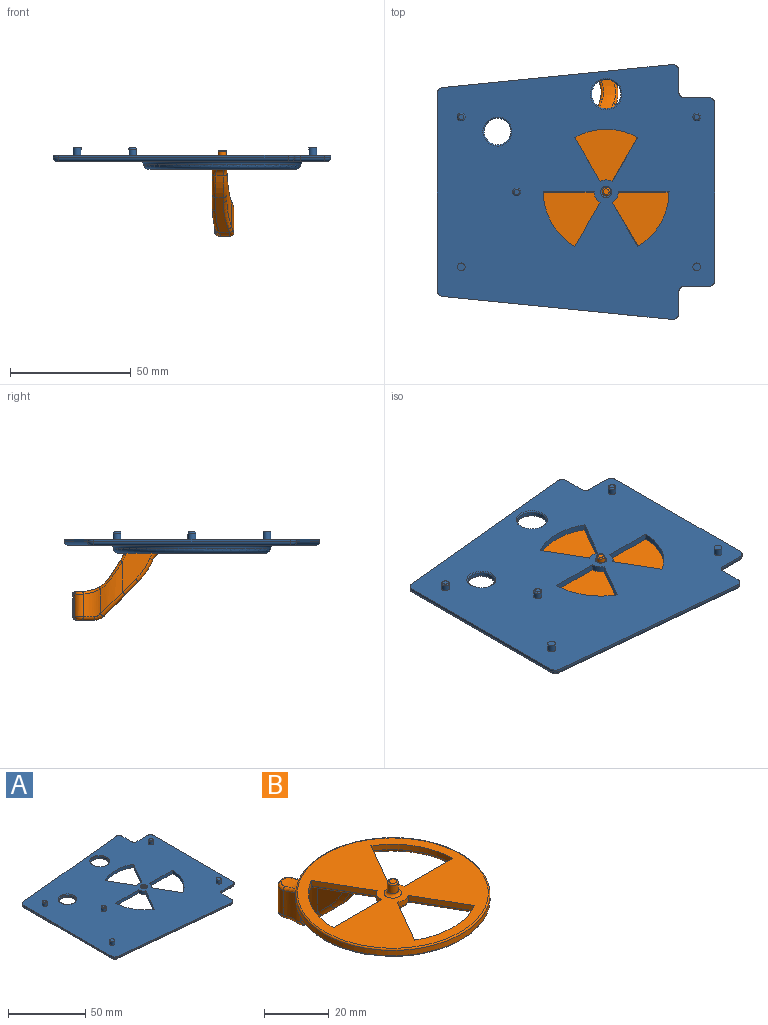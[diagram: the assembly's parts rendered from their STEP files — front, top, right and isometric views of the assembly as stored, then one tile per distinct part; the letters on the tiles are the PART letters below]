
ASSEMBLY  parts=2 mates=1
PART A: 74 faces, bbox 115x105.5x8.8 mm
  f0: plane 60.25x60.25mm, normal (0,0,-1), area 1802.9mm2, adj f9,f10,f11,f12,f13,f14,f15,f16
  f1: plane 112x102.48mm, normal (0,0,-1), area 6289.5mm2, adj f34,f35,f36,f37,f38,f39,f40,f41
  f2: plane 81.48x1mm, normal (-1,0,0), area 81.5mm2, adj f25,f26,f33,f40
  f3: plane 95x9.5mm, normal (-0.1,-1,0), area 95.5mm2, adj f25,f26,f27,f44
  f4: plane 8.74x1mm, normal (1,0,0), area 8.7mm2, adj f25,f27,f28,f48
  f5: plane 10x1mm, normal (0,-1,0), area 10mm2, adj f25,f28,f29,f47
  f6: plane 73x1mm, normal (1,0,0), area 73mm2, adj f25,f29,f30,f43
  f7: plane 10x1mm, normal (0,1,0), area 10mm2, adj f25,f30,f31,f39
  f8: plane 8.74x1mm, normal (1,0,0), area 8.7mm2, adj f25,f31,f32,f35
  f9: cylinder r=26mm len=26mm, axis (0,0,-1), area 68.1mm2, adj f0,f10,f18,f25
  f10: plane 18.19x10.5mm, normal (-0.87,0.5,0), area 52.5mm2, adj f0,f9,f11,f25
  f11: cylinder r=5mm len=5mm, axis (0,0,-1), area 13.1mm2, adj f0,f10,f18,f25
  f12: cylinder r=26mm len=22.52mm, axis (0,0,-1), area 68.1mm2, adj f0,f13,f19,f25
  f13: plane 21x2.5mm, normal (0,-1,0), area 52.5mm2, adj f0,f12,f14,f25
  f14: cylinder r=5mm len=4.33mm, axis (0,0,-1), area 13.1mm2, adj f0,f13,f19,f25
  f15: cylinder r=26mm len=22.52mm, axis (0,0,-1), area 68.1mm2, adj f0,f16,f20,f25
  f16: plane 18.19x10.5mm, normal (0.87,0.5,0), area 52.5mm2, adj f0,f15,f17,f25
  f17: cylinder r=5mm len=4.33mm, axis (0,0,-1), area 13.1mm2, adj f0,f16,f20,f25
  f18: plane 18.19x10.5mm, normal (0.87,0.5,0), area 52.5mm2, adj f0,f9,f11,f25
  f19: plane 18.19x10.5mm, normal (-0.87,0.5,0), area 52.5mm2, adj f0,f12,f14,f25
  f20: plane 21x2.5mm, normal (0,-1,0), area 52.5mm2, adj f0,f15,f17,f25
  f21: cylinder r=1.85mm len=3.7mm, axis (0,0,-1), area 11.6mm2, adj f67,f68
  f22: cylinder r=5.5mm len=11mm, axis (0,0,-1), area 51.8mm2, adj f51,f53
  f23: cylinder r=6mm len=12mm, axis (0,0,-1), area 56.5mm2, adj f50,f52
  f24: plane 95x9.5mm, normal (-0.1,1,0), area 95.5mm2, adj f25,f32,f33,f36
  f25: plane 115x105.48mm, normal (0,0,1), area 9437.3mm2, adj f2,f3,f4,f5,f6,f7,f8,f9
  f26: cylinder r=2.5mm len=2.49mm, axis (0,0,1), area 3.7mm2, adj f2,f3,f25,f42
  f27: cylinder r=2.5mm len=2.75mm, axis (0,0,-1), area 4.2mm2, adj f3,f4,f25,f46
  f28: cylinder r=2.5mm len=2.5mm, axis (0,0,-1), area 3.9mm2, adj f4,f5,f25,f49
  f29: cylinder r=2.5mm len=2.5mm, axis (0,0,-1), area 3.9mm2, adj f5,f6,f25,f45
  f30: cylinder r=2.5mm len=2.5mm, axis (0,0,-1), area 3.9mm2, adj f6,f7,f25,f41
  f31: cylinder r=2.5mm len=2.5mm, axis (0,0,1), area 3.9mm2, adj f7,f8,f25,f37
  f32: cylinder r=2.5mm len=2.75mm, axis (0,0,-1), area 4.2mm2, adj f8,f24,f25,f34
  f33: cylinder r=2.5mm len=2.49mm, axis (0,0,-1), area 3.7mm2, adj f2,f24,f25,f38
  f34: torus R=1mm, axis (0,0,1), area 7.7mm2, adj f1,f32,f35,f36
  f35: cylinder r=1.5mm len=8.74mm, axis (0,1,0), area 20.6mm2, adj f1,f8,f34,f37
  f36: cylinder r=1.5mm len=95.15mm, axis (-1,-0.1,0), area 225mm2, adj f1,f24,f34,f38
  f37: torus R=4mm, axis (0,0,1), area 11.3mm2, adj f1,f31,f35,f39
  f38: torus R=1mm, axis (0,0,1), area 6.8mm2, adj f1,f33,f36,f40
  f39: cylinder r=1.5mm len=10mm, axis (-1,0,0), area 23.6mm2, adj f1,f7,f37,f41
  f40: cylinder r=1.5mm len=81.48mm, axis (0,-1,0), area 192mm2, adj f1,f2,f38,f42
  f41: torus R=1mm, axis (0,0,1), area 7.2mm2, adj f1,f30,f39,f43
  f42: torus R=1mm, axis (0,0,1), area 6.8mm2, adj f1,f26,f40,f44
  f43: cylinder r=1.5mm len=73mm, axis (0,1,0), area 172mm2, adj f1,f6,f41,f45
  f44: cylinder r=1.5mm len=95.15mm, axis (1,-0.1,0), area 225mm2, adj f1,f3,f42,f46
  f45: torus R=1mm, axis (0,0,1), area 7.2mm2, adj f1,f29,f43,f47
  f46: torus R=1mm, axis (0,0,1), area 7.7mm2, adj f1,f27,f44,f48
  f47: cylinder r=1.5mm len=10mm, axis (1,0,0), area 23.6mm2, adj f1,f5,f45,f49
  f48: cylinder r=1.5mm len=8.74mm, axis (0,1,0), area 20.6mm2, adj f1,f4,f46,f49
  f49: torus R=4mm, axis (0,0,1), area 11.3mm2, adj f1,f28,f47,f48
  f50: torus R=6.5mm, axis (0,0,1), area 30.5mm2, adj f1,f23
  f51: torus R=6mm, axis (0,0,1), area 28mm2, adj f1,f22
  f52: torus R=6.5mm, axis (0,0,1), area 30.5mm2, adj f23,f25
  f53: torus R=6mm, axis (0,0,1), area 28mm2, adj f22,f25
  f54: cylinder r=1.62mm len=3.25mm, axis (0,0,-1), area 25.5mm2, adj f25,f66
  f55: plane 2.25x2.25mm, normal (0,0,1), area 4mm2, adj f66
  f56: cylinder r=1.62mm len=3.25mm, axis (0,0,-1), area 25.5mm2, adj f25,f65
  f57: plane 2.25x2.25mm, normal (0,0,1), area 4mm2, adj f65
  f58: cylinder r=1.62mm len=3.25mm, axis (0,0,-1), area 25.5mm2, adj f25,f64
  f59: plane 2.25x2.25mm, normal (0,0,1), area 4mm2, adj f64
  f60: cylinder r=1.62mm len=3.25mm, axis (0,0,-1), area 30.6mm2, adj f25,f61
  f61: plane 3.25x3.25mm, normal (0,0,1), area 8.3mm2, adj f60
  f62: cylinder r=1.62mm len=3.25mm, axis (0,0,-1), area 30.6mm2, adj f25,f63
  f63: plane 3.25x3.25mm, normal (0,0,1), area 8.3mm2, adj f62
  f64: torus R=1.12mm, axis (0,0,1), area 7.1mm2, adj f58,f59
  f65: torus R=1.12mm, axis (0,0,1), area 7.1mm2, adj f56,f57
  f66: torus R=1.12mm, axis (0,0,1), area 7.1mm2, adj f54,f55
  f67: torus R=2.35mm, axis (0,0,1), area 10mm2, adj f21,f25
  f68: torus R=2.85mm, axis (0,0,1), area 21.8mm2, adj f0,f21
  f69: cylinder r=8.82mm len=10.6mm, axis (0,0,1), area 17.6mm2, adj f1,f71,f73
  f70: cylinder r=30.12mm len=60.25mm, axis (0,0,1), area 529mm2, adj f0,f72
  f71: torus R=30.5mm, axis (0,0,-1), area 564.3mm2, adj f69,f72,f73
  f72: torus R=30.62mm, axis (0,0,1), area 157.6mm2, adj f70,f71
  f73: torus R=33.99mm, axis (0,0,1), area 453.4mm2, adj f1,f69,f71
PART B: 84 faces, bbox 65.1x82.2x37.1 mm
  f0: cylinder r=10mm len=11.44mm, axis (0,0,1), area 71.8mm2, adj f5,f8,f59,f60,f61,f67
  f1: cylinder r=14.79mm len=12.62mm, axis (0,0,1), area 123.8mm2, adj f6,f7,f50,f52,f63,f75
  f2: plane 59.2x58.89mm, normal (0,0,-1), area 1350.1mm2, adj f3,f4,f7,f23,f24,f25,f26,f27
  f3: torus R=29.4mm, axis (0,0,-1), area 144.6mm2, adj f2,f21,f66,f80,f83
  f4: plane 16.52x13.03mm, normal (-1,0,0), area 116.1mm2, adj f2,f8,f51,f53,f55,f71,f72,f74
  f5: cylinder r=2.8mm len=9.32mm, axis (0,0,1), area 40.1mm2, adj f0,f41,f58,f68
  f6: cylinder r=2.8mm len=9.34mm, axis (0,0,1), area 39.6mm2, adj f1,f41,f54,f73
  f7: cylinder r=28mm len=23.95mm, axis (0,0,1), area 126.3mm2, adj f1,f2,f40,f49,f77,f78,f79
  f8: cylinder r=28mm len=21.5mm, axis (0,0,1), area 100mm2, adj f0,f4,f57,f69
  f9: cylinder r=5mm len=4.31mm, axis (0,0,1), area 10.5mm2, adj f10,f18,f22,f23
  f10: plane 21x2mm, normal (0,1,0), area 42mm2, adj f9,f11,f22,f25
  f11: cylinder r=26mm len=22.5mm, axis (0,0,1), area 54.5mm2, adj f10,f18,f22,f26
  f12: cylinder r=5mm len=5mm, axis (0,0,1), area 10.5mm2, adj f13,f19,f22,f31
  f13: plane 18.19x10.5mm, normal (0.87,-0.5,0), area 42mm2, adj f12,f14,f22,f33
  f14: cylinder r=26mm len=26mm, axis (0,0,1), area 54.5mm2, adj f13,f19,f22,f34
  f15: plane 21x2mm, normal (0,1,0), area 42mm2, adj f16,f20,f22,f27
  f16: cylinder r=5mm len=4.35mm, axis (0,0,1), area 10.5mm2, adj f15,f17,f22,f28
  f17: plane 18.19x10.5mm, normal (-0.87,-0.5,0), area 42mm2, adj f16,f20,f22,f30
  f18: plane 18.19x10.5mm, normal (0.87,-0.5,0), area 42mm2, adj f9,f11,f22,f24
  f19: plane 18.19x10.5mm, normal (-0.87,-0.5,0), area 42mm2, adj f12,f14,f22,f32
  f20: cylinder r=26mm len=22.53mm, axis (0,0,1), area 54.5mm2, adj f15,f17,f22,f29
  f21: cylinder r=29.9mm len=59.8mm, axis (0,0,1), area 375.7mm2, adj f3,f39
  f22: plane 58.8x58.8mm, normal (0,0,1), area 1670mm2, adj f9,f10,f11,f12,f13,f14,f15,f16
  f23: torus R=4mm, axis (0,0,-1), area 9.4mm2, adj f2,f9,f24,f25
  f24: cylinder r=1mm len=20.52mm, axis (0.5,0.87,0), area 34.6mm2, adj f2,f18,f23,f26
  f25: cylinder r=1mm len=23.1mm, axis (-1,0,0), area 34.6mm2, adj f2,f10,f23,f26
  f26: torus R=27mm, axis (0,0,-1), area 44.9mm2, adj f2,f11,f24,f25
  f27: cylinder r=1mm len=23.12mm, axis (-1,0,0), area 34.6mm2, adj f2,f15,f28,f29
  f28: torus R=4mm, axis (0,0,-1), area 9.4mm2, adj f2,f16,f27,f30
  f29: torus R=27mm, axis (0,0,-1), area 44.9mm2, adj f2,f20,f27,f30
  f30: cylinder r=1mm len=20.51mm, axis (0.5,-0.87,0), area 34.6mm2, adj f2,f17,f28,f29
  f31: torus R=4mm, axis (0,0,-1), area 9.4mm2, adj f2,f12,f32,f33
  f32: cylinder r=1mm len=20.52mm, axis (0.5,-0.87,0), area 34.6mm2, adj f2,f19,f31,f34
  f33: cylinder r=1mm len=20.51mm, axis (0.5,0.87,0), area 34.6mm2, adj f2,f13,f31,f34
  f34: torus R=27mm, axis (0,0,-1), area 44.9mm2, adj f2,f14,f32,f33
  f35: cylinder r=1.7mm len=3.4mm, axis (0,0,-1), area 32mm2, adj f37,f38
  f36: plane 2.4x2.4mm, normal (0,0,1), area 4.5mm2, adj f37
  f37: torus R=1.2mm, axis (0,0,-1), area 7.5mm2, adj f35,f36
  f38: torus R=2.7mm, axis (0,0,-1), area 20.4mm2, adj f22,f35
  f39: torus R=29.4mm, axis (0,0,-1), area 146.7mm2, adj f21,f22
  f40: plane 13.01x9.52mm, normal (1,0,0), area 67.6mm2, adj f2,f7,f46,f47,f48
  f41: plane 9.34x0.98mm, normal (-0.41,0.91,0), area 10mm2, adj f5,f6,f56,f70
  f42: plane 7.69x4.89mm, normal (0,0,-1), area 28.4mm2, adj f52,f54,f56,f58,f60,f62
  f43: plane 14.41x14.41mm, normal (0,-0.71,-0.71), area 70.4mm2, adj f44,f48,f49,f50,f55,f57,f59,f62
  f44: cylinder r=28mm len=9.05mm, axis (1,0,0), area 32.9mm2, adj f43,f45,f47,f53
  f45: cylinder r=5mm len=4.62mm, axis (1,0,0), area 17.6mm2, adj f2,f44,f46,f51
  f46: torus R=6.5mm, axis (-1,0,0), area 10.6mm2, adj f2,f40,f45,f47
  f47: torus R=26.5mm, axis (-1,0,0), area 25.3mm2, adj f40,f44,f46,f48
  f48: cylinder r=1.5mm len=3mm, axis (0,0.71,-0.71), area 6.4mm2, adj f40,f43,f47,f49
  f49: bspline ~18.67x18.03mm, area 33.3mm2, adj f7,f43,f48,f50
  f50: bspline ~5.64x5.52mm, area 4.6mm2, adj f1,f43,f49,f63
  f51: torus R=6.5mm, axis (-1,0,0), area 10.6mm2, adj f2,f4,f45,f53
  f52: torus R=13.29mm, axis (0,0,-1), area 18.2mm2, adj f1,f42,f54,f63
  f53: torus R=26.5mm, axis (-1,0,0), area 25.3mm2, adj f4,f44,f51,f55
  f54: torus R=1.3mm, axis (0,0,-1), area 8.1mm2, adj f6,f42,f52,f56
  f55: cylinder r=1.5mm len=6.51mm, axis (0,0.71,-0.71), area 18.2mm2, adj f4,f43,f53,f57
  f56: cylinder r=1.5mm len=1.81mm, axis (-0.91,-0.41,0), area 2.5mm2, adj f41,f42,f54,f58
  f57: bspline ~14.1x13.87mm, area 32.2mm2, adj f8,f43,f55,f59
  f58: torus R=1.3mm, axis (0,0,-1), area 8.2mm2, adj f5,f42,f56,f60
  f59: bspline ~1.75x1.52mm, area 0.8mm2, adj f0,f43,f57,f61
  f60: torus R=11.5mm, axis (0,0,-1), area 12mm2, adj f0,f42,f58,f61
  f61: bspline ~5.01x2.8mm, area 8.4mm2, adj f0,f59,f60,f62
  f62: cylinder r=5mm len=4.46mm, axis (1,0,0), area 15.7mm2, adj f42,f43,f61,f63
  f63: bspline ~4.85x3.03mm, area 8.2mm2, adj f1,f50,f52,f62
  f64: extruded ~19.89x15.63mm, area 127.3mm2, adj f67,f68,f69,f70,f72,f73,f75,f76
  f65: plane 4.08x0.45mm, normal (0,1,0), area 1.8mm2, adj f66,f71,f76,f79
  f66: plane 9.1x1.35mm, normal (0,0,-1), area 11.2mm2, adj f3,f65,f80,f81,f82,f83
  f67: bspline ~9.69x3.78mm, area 11.8mm2, adj f0,f64,f68,f69
  f68: bspline ~4.17x2.41mm, area 5.9mm2, adj f5,f64,f67,f70
  f69: bspline ~13.53x11.61mm, area 21.2mm2, adj f8,f64,f67,f72
  f70: bspline ~6.42x3.59mm, area 1.7mm2, adj f41,f64,f68,f73
  f71: cylinder r=1mm len=1mm, axis (0,0,-1), area 0.6mm2, adj f2,f4,f65,f74,f81
  f72: bspline ~4.11x2.41mm, area 4.8mm2, adj f4,f64,f69,f74
  f73: bspline ~4.2x2.29mm, area 6mm2, adj f6,f64,f70,f75
  f74: torus R=2mm, axis (-1,0,0), area 0.4mm2, adj f4,f71,f72,f76
  f75: bspline ~14.56x5.86mm, area 20.2mm2, adj f1,f64,f73,f77
  f76: cylinder r=1mm len=4.08mm, axis (-1,0,0), area 0.8mm2, adj f64,f65,f74,f78
  f77: bspline ~14.47x10.4mm, area 26.8mm2, adj f7,f64,f75,f78
  f78: bspline ~1.16x1.09mm, area 0.4mm2, adj f7,f76,f77,f79
  f79: cylinder r=1mm len=1.08mm, axis (0,0,1), area 0.7mm2, adj f2,f7,f65,f78,f82
  f80: cylinder r=1mm len=1.38mm, axis (0,1,0), area 0.3mm2, adj f2,f3,f66,f81
  f81: cylinder r=1mm len=1.3mm, axis (1,0,0), area 0.2mm2, adj f2,f66,f71,f80
  f82: cylinder r=1mm len=4.32mm, axis (1,0,0), area 1.2mm2, adj f2,f66,f79,f83
  f83: cylinder r=1mm len=1.21mm, axis (0,1,0), area 0.3mm2, adj f2,f3,f66,f82
PLACE A at identity fixed
PLACE B rot(axis=(0,0,1),0.3deg) t=(0,-0.2,0)mm
MATE revolute B.f3 <-> A.f0  axis (0,0,1) through (70,0.12,0)mm
